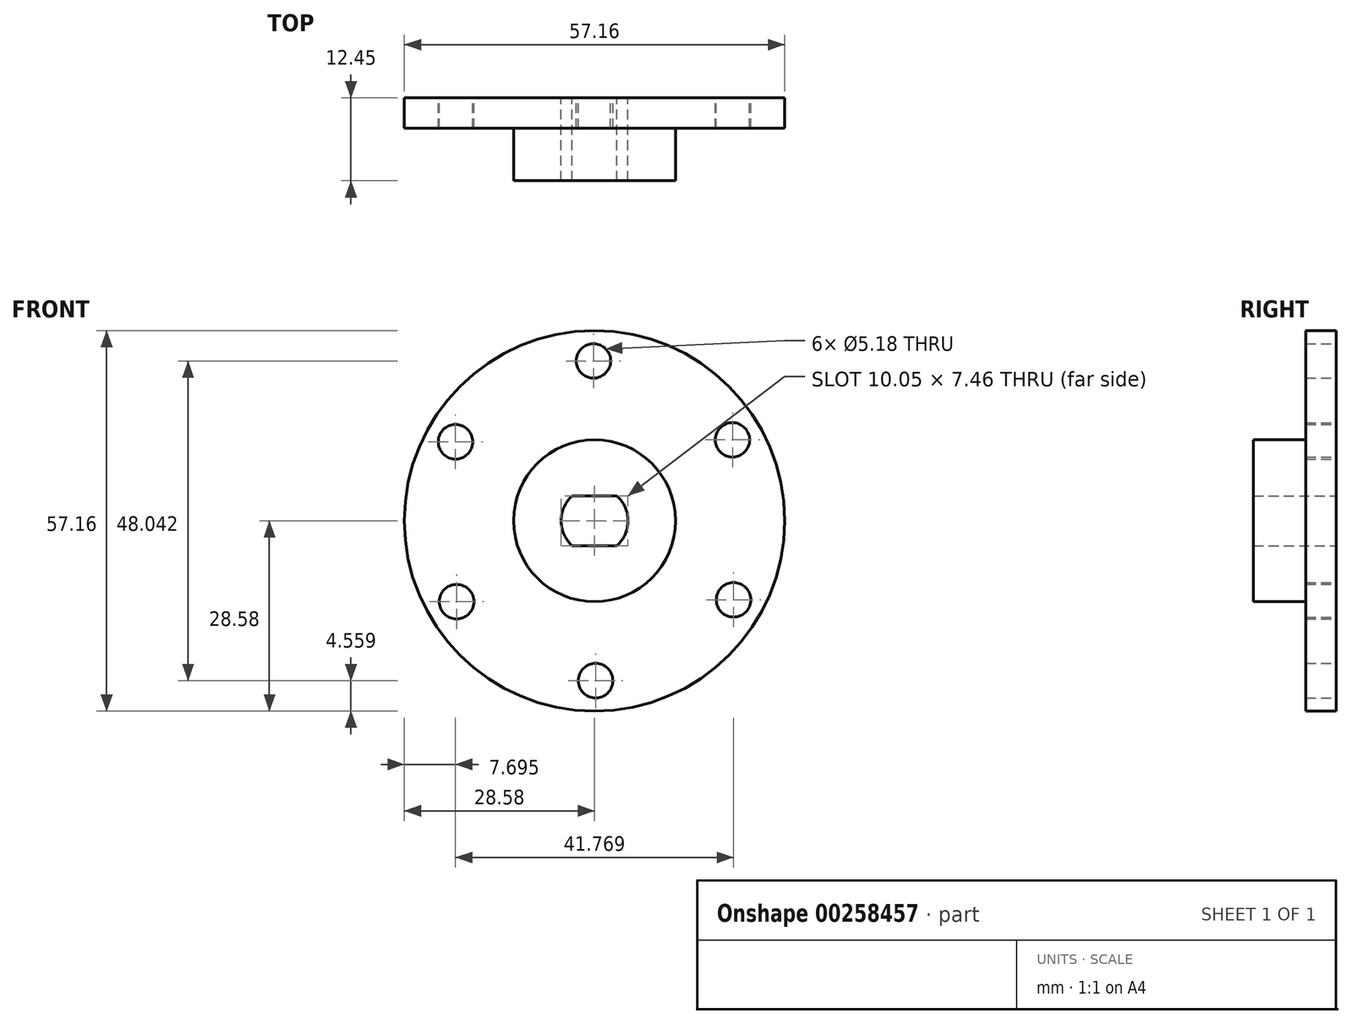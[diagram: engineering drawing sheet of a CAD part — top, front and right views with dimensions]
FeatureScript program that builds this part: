
annotation { "Feature Type Name" : "Feature", "Feature Type Description" : "" }
export const myFeature = defineFeature(function(context is Context, id is Id, definition is map)
    precondition{}
    {
        {
            var Q0;
            Q0=qCreatedBy(makeId("Front.planeOp"),FACE);
            var sketch = newSketch(context, id + "F0", { "sketchPlane" : qUnion([Q0])});
            skCircle(sketch, "E0", {"center": v(0, 0) * mm, "radius": 28.58 * mm});
            skLineSegment(sketch, "E1.0", {"start": v(20.88, -11.87) * mm, "end": v(20.52, -12.08) * mm});
            skLineSegment(sketch, "E1.1", {"start": v(0.16, -24.02) * mm, "end": v(-0.2, -23.81) * mm});
            skLineSegment(sketch, "E1.2", {"start": v(-20.72, -12.15) * mm, "end": v(-20.72, -11.73) * mm});
            skLineSegment(sketch, "E1.3", {"start": v(-20.88, 11.87) * mm, "end": v(-20.52, 12.08) * mm});
            skLineSegment(sketch, "E1.4", {"start": v(-0.16, 24.02) * mm, "end": v(0.2, 23.81) * mm});
            skLineSegment(sketch, "E1.5", {"start": v(20.72, 12.15) * mm, "end": v(20.72, 11.73) * mm});
            skCircle(sketch, "E2", {"center": v(-0.16, 24.02) * mm, "radius": 2.6 * mm});
            skCircle(sketch, "E3", {"center": v(20.72, 12.15) * mm, "radius": 2.6 * mm});
            skCircle(sketch, "E4", {"center": v(20.88, -11.87) * mm, "radius": 2.6 * mm});
            skCircle(sketch, "E5", {"center": v(0.16, -24.02) * mm, "radius": 2.6 * mm});
            skCircle(sketch, "E6", {"center": v(-20.72, -12.15) * mm, "radius": 2.6 * mm});
            skCircle(sketch, "E7", {"center": v(-20.88, 11.87) * mm, "radius": 2.6 * mm});
            skLineSegment(sketch, "E8.trimOffspring", {"start": v(-0.53, 23.8) * mm, "end": v(-0.16, 24.02) * mm});
            skLineSegment(sketch, "E9.trimOffspring", {"start": v(-20.88, 11.45) * mm, "end": v(-20.88, 11.87) * mm});
            skLineSegment(sketch, "E10.trimOffspring", {"start": v(-20.35, -12.36) * mm, "end": v(-20.72, -12.15) * mm});
            skLineSegment(sketch, "E11.trimOffspring", {"start": v(0.53, -23.8) * mm, "end": v(0.16, -24.02) * mm});
            skLineSegment(sketch, "E12.trimOffspring", {"start": v(20.88, -11.45) * mm, "end": v(20.88, -11.87) * mm});
            skLineSegment(sketch, "E13.trimOffspring", {"start": v(20.35, 12.36) * mm, "end": v(20.72, 12.15) * mm});
            skCircle(sketch, "E14", {"center": v(0, 0) * mm, "radius": 12.17 * mm});
            skArc(sketch, "E15", {"start": v(-3.37, 3.73) * mm, "mid": v(-5.02, 0) * mm, "end": v(-3.37, -3.73) * mm});
            skLineSegment(sketch, "E16.bottom", {"start": v(3.37, -3.73) * mm, "end": v(-3.37, -3.73) * mm});
            skLineSegment(sketch, "E16.top", {"start": v(3.37, 3.73) * mm, "end": v(-3.37, 3.73) * mm});
            skArc(sketch, "E17.trimOffspring", {"start": v(3.37, -3.73) * mm, "mid": v(5.02, 0) * mm, "end": v(3.37, 3.73) * mm});
            skSolve(sketch);
        }
        {
            var Q0;
            Q0=makeQuery(id+"F0.imprint","IMPRINT",FACE,{"disambiguationData":[TD([[makeQuery(id+"F0.imprint","IMPRINT",EDGE,{"derivedFrom":sQuery(id+"F0.wireOp",EDGE,"E0")}),1.0]])]});
            extrude(context, id + "F1", {"entities" : qUnion([Q0]), "depth" : 4.57 * mm});
        }
        {
            var Q0;
            Q0=makeQuery(id+"F0.imprint","IMPRINT",FACE,{"disambiguationData":[TD([[makeQuery(id+"F0.imprint","IMPRINT",EDGE,{"derivedFrom":sQuery(id+"F0.wireOp",EDGE,"E14")}),1.0]])]});
            extrude(context, id + "F2", {"entities" : qUnion([Q0]), "operationType" : NewBodyOperationType.ADD, "depth" : 12.45 * mm});
        }
    });
